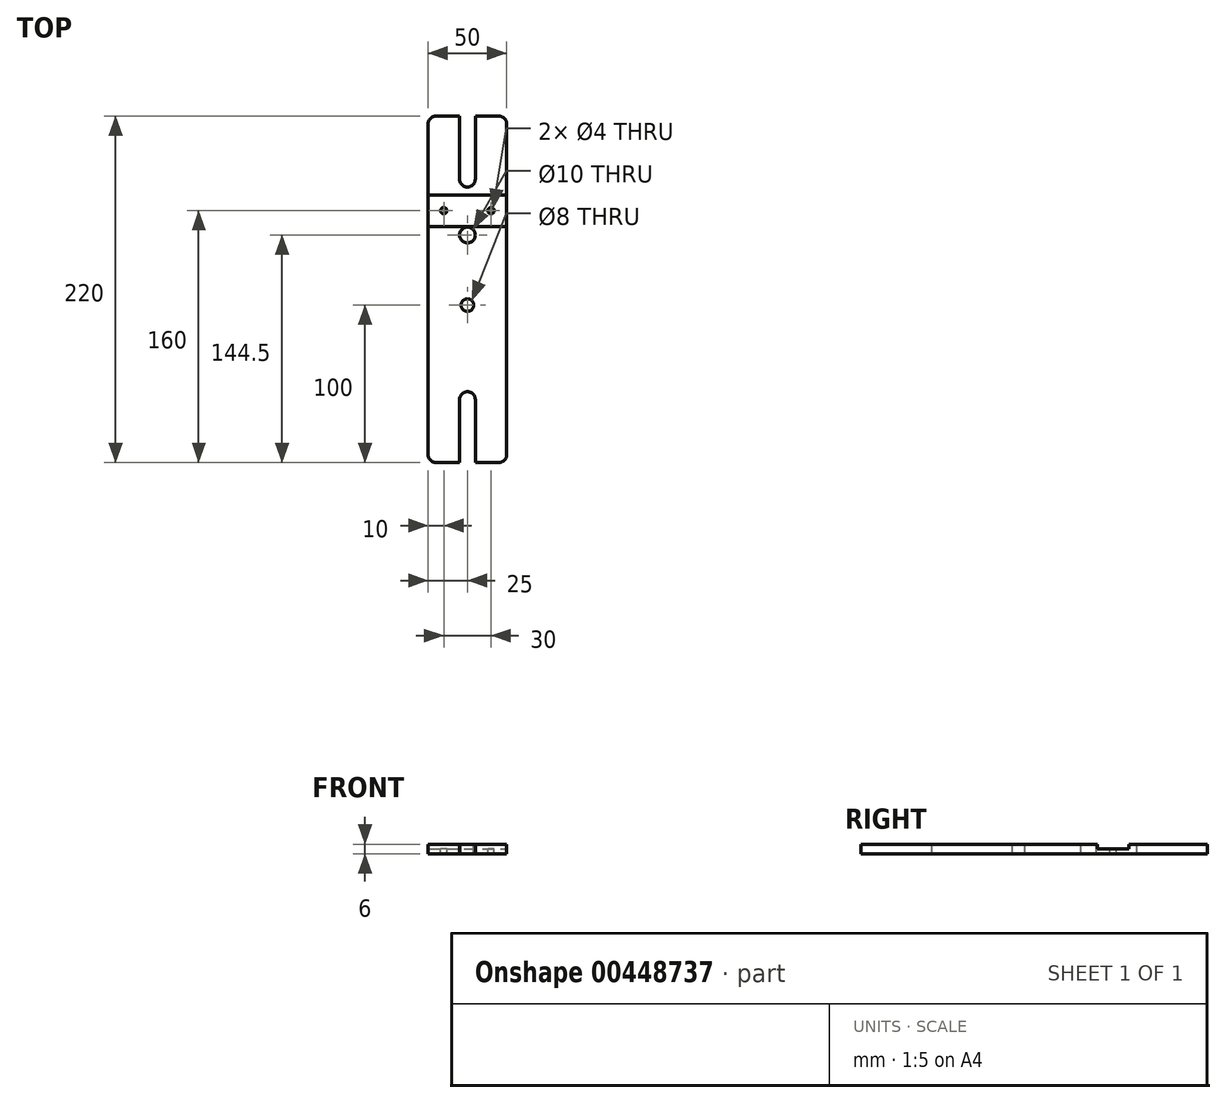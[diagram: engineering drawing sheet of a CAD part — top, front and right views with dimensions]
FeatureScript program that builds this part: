
annotation { "Feature Type Name" : "Feature", "Feature Type Description" : "" }
export const myFeature = defineFeature(function(context is Context, id is Id, definition is map)
    precondition{}
    {
        {
            var Q0;
            Q0=qCreatedBy(makeId("Top.planeOp"),FACE);
            var sketch = newSketch(context, id + "F0", { "sketchPlane" : qUnion([Q0])});
            skLineSegment(sketch, "E0.bottom", {"start": v(-20, 110) * mm, "end": v(20, 110) * mm});
            skLineSegment(sketch, "E0.top", {"start": v(-20, -110) * mm, "end": v(20, -110) * mm});
            skLineSegment(sketch, "E0.left", {"start": v(-25, 105) * mm, "end": v(-25, -105) * mm});
            skLineSegment(sketch, "E0.right", {"start": v(25, 105) * mm, "end": v(25, -105) * mm});
            skPoint(sketch, "E0.middle", {"position": v(0, 0) * mm});
            skPoint(sketch, "E1.visualSharp", {"position": v(-25, -110) * mm});
            skArc(sketch, "E1.filletArc", {"start": v(-25, -105) * mm, "mid": v(-23.54, -108.54) * mm, "end": v(-20, -110) * mm});
            skPoint(sketch, "E2.visualSharp", {"position": v(25, -110) * mm});
            skArc(sketch, "E2.filletArc", {"start": v(20, -110) * mm, "mid": v(23.54, -108.54) * mm, "end": v(25, -105) * mm});
            skPoint(sketch, "E3.visualSharp", {"position": v(25, 110) * mm});
            skArc(sketch, "E3.filletArc", {"start": v(25, 105) * mm, "mid": v(23.54, 108.54) * mm, "end": v(20, 110) * mm});
            skPoint(sketch, "E4.visualSharp", {"position": v(-25, 110) * mm});
            skArc(sketch, "E4.filletArc", {"start": v(-20, 110) * mm, "mid": v(-23.54, 108.54) * mm, "end": v(-25, 105) * mm});
            skSolve(sketch);
        }
        {
            var Q0;
            Q0=makeQuery(id+"F0.imprint","IMPRINT",FACE,{"disambiguationData":[TD([[makeQuery(id+"F0.imprint","IMPRINT",EDGE,{"derivedFrom":sQuery(id+"F0.wireOp",EDGE,"E0.bottom")}),-1.0]])]});
            extrude(context, id + "F1", {"entities" : qUnion([Q0]), "depth" : 6 * mm});
        }
        {
            var Q0;
            Q0=makeQuery(id+"F1.opExtrude","CAP_FACE",FACE,{"disambiguationData":[OSD([sQuery(id+"F0.wireOp",EDGE,"E0.bottom"),sQuery(id+"F0.wireOp",EDGE,"E0.top"),sQuery(id+"F0.wireOp",EDGE,"E0.left"),sQuery(id+"F0.wireOp",EDGE,"E0.right"),sQuery(id+"F0.wireOp",EDGE,"E1.filletArc"),sQuery(id+"F0.wireOp",EDGE,"E2.filletArc"),sQuery(id+"F0.wireOp",EDGE,"E3.filletArc"),sQuery(id+"F0.wireOp",EDGE,"E4.filletArc")])],"isStart":false});
            var sketch = newSketch(context, id + "F2", { "sketchPlane" : qUnion([Q0])});
            skLineSegment(sketch, "E5", {"start": v(25, -97.82) * mm, "end": v(-25, -97.82) * mm});
            skLineSegment(sketch, "E6", {"start": v(25, 82.4) * mm, "end": v(-25, 82.4) * mm});
            skLineSegment(sketch, "E7", {"start": v(10.41, 110) * mm, "end": v(10.41, -110) * mm});
            skPoint(sketch, "E7.endSnap0", {"position": v(0, -110) * mm});
            skLineSegment(sketch, "E8", {"start": v(5, -110) * mm, "end": v(5, -70) * mm});
            skLineSegment(sketch, "E9", {"start": v(-5, -110) * mm, "end": v(-5, -70) * mm});
            skArc(sketch, "E10", {"start": v(5, -70) * mm, "mid": v(0, -65) * mm, "end": v(-5, -70) * mm});
            skLineSegment(sketch, "E11", {"start": v(5, 110) * mm, "end": v(5, 70) * mm});
            skLineSegment(sketch, "E12", {"start": v(-5, 110) * mm, "end": v(-5, 70) * mm});
            skArc(sketch, "E13", {"start": v(-5, 70) * mm, "mid": v(0, 65) * mm, "end": v(5, 70) * mm});
            skCircle(sketch, "E14", {"center": v(-15, 50) * mm, "radius": 2 * mm});
            skCircle(sketch, "E15", {"center": v(15, 50) * mm, "radius": 2 * mm});
            skLineSegment(sketch, "E16", {"start": v(-15, 110) * mm, "end": v(-15, 60) * mm});
            skLineSegment(sketch, "E17", {"start": v(-25, 60) * mm, "end": v(25, 60) * mm});
            skLineSegment(sketch, "E18", {"start": v(25, 60) * mm, "end": v(25, 40) * mm});
            skLineSegment(sketch, "E19", {"start": v(25, 40) * mm, "end": v(-25, 40) * mm});
            skLineSegment(sketch, "E20", {"start": v(-25, 60) * mm, "end": v(-25, 40) * mm});
            skLineSegment(sketch, "E21", {"start": v(16.2, 110) * mm, "end": v(16.2, 34.5) * mm});
            skLineSegment(sketch, "E22", {"start": v(25, 34.5) * mm, "end": v(0, 34.5) * mm});
            skCircle(sketch, "E23", {"center": v(0, 34.5) * mm, "radius": 5 * mm});
            skLineSegment(sketch, "E24", {"start": v(15.95, -110) * mm, "end": v(15.95, -10) * mm});
            skLineSegment(sketch, "E25", {"start": v(25, -10) * mm, "end": v(0, -10) * mm});
            skCircle(sketch, "E26", {"center": v(0, -10) * mm, "radius": 4 * mm});
            skSolve(sketch);
        }
        {
            var Q0;
            {var subQ0=sQuery(id+"F2.wireOp",EDGE,"E8");var subQ1=sQuery(id+"F2.wireOp",EDGE,"E5");var subQ2=makeQuery(id+"F2.imprint","INTERSECT",VERTEX,{"derivedFrom":[subQ1,subQ0]});Q0=makeQuery(id+"F2.imprint","IMPRINT",FACE,{"disambiguationData":[TD([[makeQuery(id+"F2.imprint","IMPRINT",EDGE,{"disambiguationData":[TD([[subQ2,-1.0]])],"derivedFrom":subQ1}),1.0]])]});}
            var Q1;
            {var subQ5=sQuery(id+"F2.wireOp",EDGE,"E10");Q1=makeQuery(id+"F2.imprint","IMPRINT",FACE,{"disambiguationData":[TD([[makeQuery(id+"F2.imprint","IMPRINT",EDGE,{"derivedFrom":subQ5}),1.0]])]});}
            var Q2;
            Q2=makeQuery(id+"F2.imprint","IMPRINT",FACE,{"disambiguationData":[TD([[makeQuery(id+"F2.imprint","IMPRINT",EDGE,{"derivedFrom":sQuery(id+"F2.wireOp",EDGE,"E26")}),1.0]])]});
            var Q3;
            Q3=makeQuery(id+"F2.imprint","IMPRINT",FACE,{"disambiguationData":[TD([[makeQuery(id+"F2.imprint","IMPRINT",EDGE,{"derivedFrom":sQuery(id+"F2.wireOp",EDGE,"E23")}),1.0]])]});
            var Q4;
            Q4=makeQuery(id+"F2.imprint","IMPRINT",FACE,{"disambiguationData":[TD([[makeQuery(id+"F2.imprint","IMPRINT",EDGE,{"derivedFrom":sQuery(id+"F2.wireOp",EDGE,"E14")}),1.0]])]});
            var Q5;
            {var subQ0=sQuery(id+"F2.wireOp",EDGE,"E21");var subQ1=sQuery(id+"F2.wireOp",EDGE,"E15");var subQ2=makeQuery(id+"F2.imprint","INTERSECT",VERTEX,{"disambiguationData":[OD(0.0)],"derivedFrom":[subQ1,subQ0]});Q5=makeQuery(id+"F2.imprint","IMPRINT",FACE,{"disambiguationData":[TD([[makeQuery(id+"F2.imprint","IMPRINT",EDGE,{"disambiguationData":[TD([[subQ2,-1.0]])],"derivedFrom":subQ1}),1.0]])]});}
            var Q6;
            {var subQ5=sQuery(id+"F2.wireOp",EDGE,"E13");Q6=makeQuery(id+"F2.imprint","IMPRINT",FACE,{"disambiguationData":[TD([[makeQuery(id+"F2.imprint","IMPRINT",EDGE,{"derivedFrom":subQ5}),1.0]])]});}
            var Q7;
            {var subQ0=sQuery(id+"F2.wireOp",EDGE,"E11");var subQ1=sQuery(id+"F2.wireOp",EDGE,"E6");var subQ2=makeQuery(id+"F2.imprint","INTERSECT",VERTEX,{"derivedFrom":[subQ1,subQ0]});Q7=makeQuery(id+"F2.imprint","IMPRINT",FACE,{"disambiguationData":[TD([[makeQuery(id+"F2.imprint","IMPRINT",EDGE,{"disambiguationData":[TD([[subQ2,-1.0]])],"derivedFrom":subQ1}),-1.0]])]});}
            var Q8;
            {var subQ0=sQuery(id+"F2.wireOp",EDGE,"E21");var subQ1=sQuery(id+"F2.wireOp",EDGE,"E15");var subQ2=makeQuery(id+"F2.imprint","INTERSECT",VERTEX,{"disambiguationData":[OD(0.0)],"derivedFrom":[subQ1,subQ0]});Q8=makeQuery(id+"F2.imprint","IMPRINT",FACE,{"disambiguationData":[TD([[makeQuery(id+"F2.imprint","IMPRINT",EDGE,{"disambiguationData":[TD([[subQ2,1.0]])],"derivedFrom":subQ1}),1.0]])]});}
            extrude(context, id + "F3", {"entities" : qUnion([Q0, Q1, Q2, Q3, Q4, Q5, Q6, Q7, Q8]), "operationType" : NewBodyOperationType.REMOVE, "oppositeDirection" : true, "depth" : 25 * mm});
        }
        {
            var Q0;
            Q0=makeQuery(id+"F1.opExtrude","CAP_FACE",FACE,{"disambiguationData":[OSD([sQuery(id+"F0.wireOp",EDGE,"E0.bottom"),sQuery(id+"F0.wireOp",EDGE,"E0.top"),sQuery(id+"F0.wireOp",EDGE,"E0.left"),sQuery(id+"F0.wireOp",EDGE,"E0.right"),sQuery(id+"F0.wireOp",EDGE,"E1.filletArc"),sQuery(id+"F0.wireOp",EDGE,"E2.filletArc"),sQuery(id+"F0.wireOp",EDGE,"E3.filletArc"),sQuery(id+"F0.wireOp",EDGE,"E4.filletArc")])],"isStart":false});
            var sketch = newSketch(context, id + "F4", { "sketchPlane" : qUnion([Q0])});
            skLineSegment(sketch, "E27", {"start": v(12.5, 110) * mm, "end": v(12.5, 60) * mm});
            skLineSegment(sketch, "E28", {"start": v(12.5, 60) * mm, "end": v(25, 60) * mm});
            skLineSegment(sketch, "E29.bottom", {"start": v(25, 60) * mm, "end": v(-25, 60) * mm});
            skLineSegment(sketch, "E29.top", {"start": v(25, 40) * mm, "end": v(-25, 40) * mm});
            skLineSegment(sketch, "E29.left", {"start": v(25, 60) * mm, "end": v(25, 40) * mm});
            skLineSegment(sketch, "E29.right", {"start": v(-25, 60) * mm, "end": v(-25, 40) * mm});
            skSolve(sketch);
        }
        {
            var Q0;
            Q0 = qSketchRegion(id + "F4", true);
            extrude(context, id + "F5", {"entities" : qUnion([Q0]), "operationType" : NewBodyOperationType.REMOVE, "oppositeDirection" : true, "depth" : 3 * mm});
        }
    });
